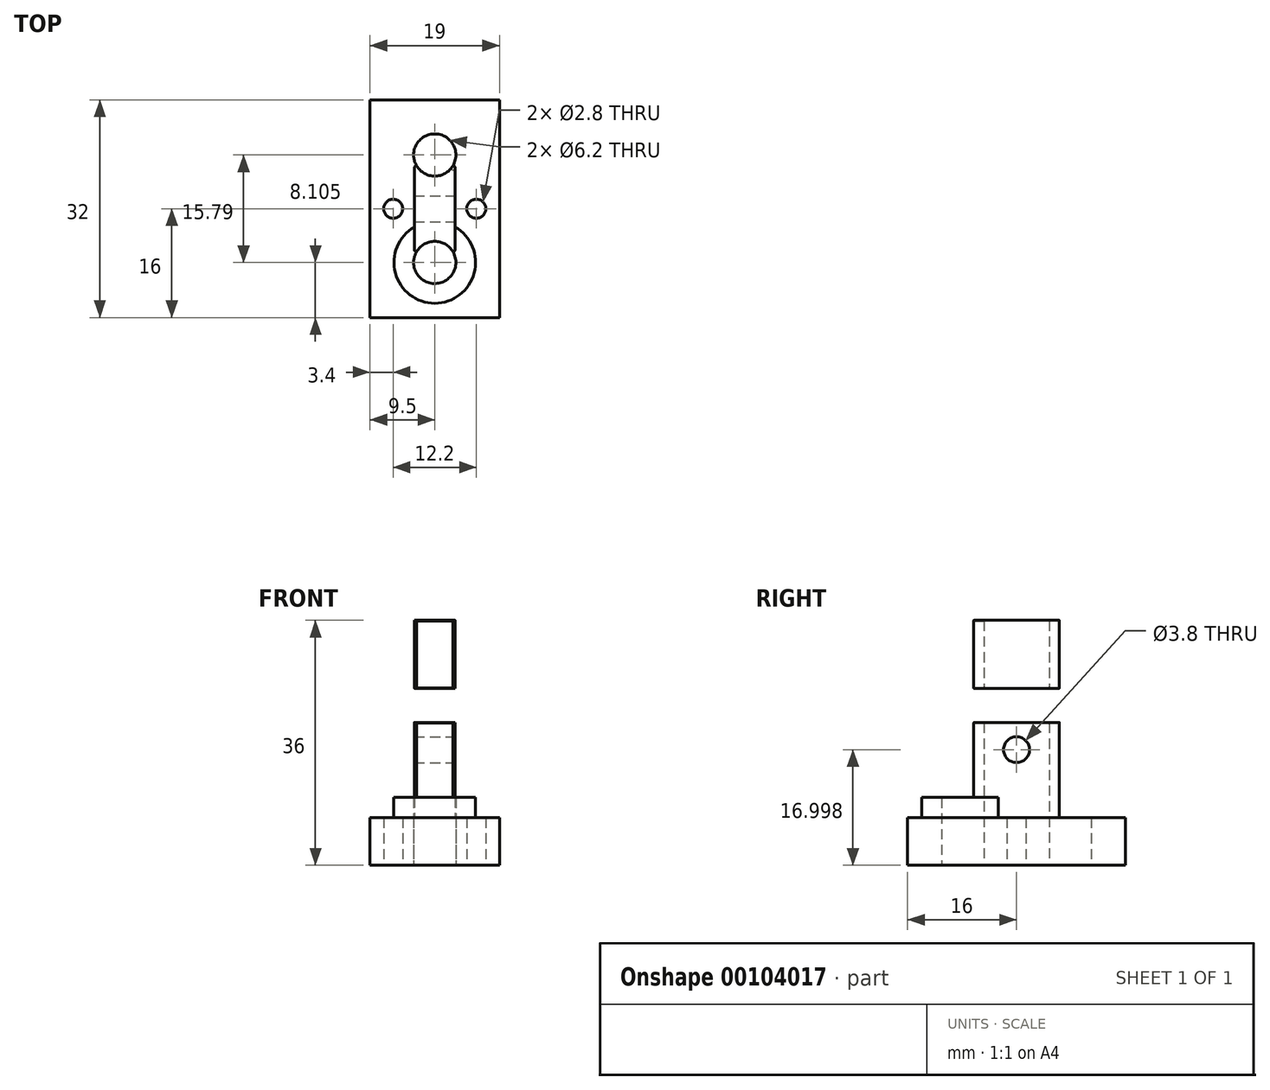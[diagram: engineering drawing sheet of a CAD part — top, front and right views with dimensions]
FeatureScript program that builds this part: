
annotation { "Feature Type Name" : "Feature", "Feature Type Description" : "" }
export const myFeature = defineFeature(function(context is Context, id is Id, definition is map)
    precondition{}
    {
        {
            var Q0;
            Q0=qCreatedBy(makeId("Top.planeOp"),FACE);
            var sketch = newSketch(context, id + "F0", { "sketchPlane" : qUnion([Q0])});
            skCircle(sketch, "E0", {"center": v(0, -7.9) * mm, "radius": 3 * mm});
            skLineSegment(sketch, "E1", {"start": v(-3.1, 0) * mm, "end": v(4.43, 0) * mm, "construction": true});
            skCircle(sketch, "E2.MirrorC", {"center": v(0, 7.9) * mm, "radius": 3 * mm});
            skLineSegment(sketch, "E3", {"start": v(-4.67, -18.12) * mm, "end": v(4.3, -18.12) * mm, "construction": true});
            skCircle(sketch, "E4.MirrorC", {"center": v(0, -28.36) * mm, "radius": 3 * mm, "construction": true});
            skLineSegment(sketch, "E5.MirrorCS", {"start": v(-4.67, 18.12) * mm, "end": v(4.3, 18.12) * mm, "construction": true});
            skLineSegment(sketch, "E6", {"start": v(-3, -7.9) * mm, "end": v(-3, 7.9) * mm});
            skLineSegment(sketch, "E7", {"start": v(3, -7.9) * mm, "end": v(3, 7.9) * mm});
            skArc(sketch, "E8", {"start": v(-3, -2.7) * mm, "mid": v(0, -13.9) * mm, "end": v(3, -2.7) * mm});
            skArc(sketch, "E9.MirrorCS", {"start": v(-3, 2.7) * mm, "mid": v(0, 13.9) * mm, "end": v(3, 2.7) * mm});
            skSolve(sketch);
        }
        {
            var Q0;
            {var subQ5=sQuery(id+"F0.wireOp",EDGE,"E8");Q0=makeQuery(id+"F0.imprint","IMPRINT",FACE,{"disambiguationData":[TD([[makeQuery(id+"F0.imprint","IMPRINT",EDGE,{"derivedFrom":subQ5}),1.0]])]});}
            var Q1;
            {var subQ1=sQuery(id+"F0.wireOp",EDGE,"E6");var subQ5=sQuery(id+"F0.wireOp",EDGE,"E0");var subQ6=makeQuery(id+"F0.imprint","INTERSECT",VERTEX,{"derivedFrom":[subQ5,subQ1]});Q1=makeQuery(id+"F0.imprint","IMPRINT",FACE,{"disambiguationData":[TD([[makeQuery(id+"F0.imprint","IMPRINT",EDGE,{"disambiguationData":[TD([[subQ6,1.0]])],"derivedFrom":subQ5}),-1.0]])]});}
            var Q2;
            {var subQ5=sQuery(id+"F0.wireOp",EDGE,"E9.MirrorCS");Q2=makeQuery(id+"F0.imprint","IMPRINT",FACE,{"disambiguationData":[TD([[makeQuery(id+"F0.imprint","IMPRINT",EDGE,{"derivedFrom":subQ5}),-1.0]])]});}
            extrude(context, id + "F1", {"entities" : qUnion([Q0, Q1, Q2]), "depth" : 10 * mm});
        }
        {
            var Q0;
            {var subQ1=sQuery(id+"F0.wireOp",EDGE,"E6");var subQ5=sQuery(id+"F0.wireOp",EDGE,"E0");var subQ6=makeQuery(id+"F0.imprint","INTERSECT",VERTEX,{"derivedFrom":[subQ5,subQ1]});Q0=makeQuery(id+"F0.imprint","IMPRINT",FACE,{"disambiguationData":[TD([[makeQuery(id+"F0.imprint","IMPRINT",EDGE,{"disambiguationData":[TD([[subQ6,1.0]])],"derivedFrom":subQ5}),-1.0]])]});}
            extrude(context, id + "F2", {"entities" : qUnion([Q0]), "operationType" : NewBodyOperationType.ADD, "depth" : 21 * mm});
        }
        {
            var Q0;
            {var subQ0=sQuery(id+"F0.wireOp",EDGE,"E7");Q0=makeQuery(id+"F2.boolean.opBoolean","MERGE",FACE,{"derivedFrom":[makeQuery(id+"F1.opExtrude","SWEPT_FACE",FACE,{"disambiguationData":[OSD([subQ0])]}),makeQuery(id+"F2.opExtrude","SWEPT_FACE",FACE,{"disambiguationData":[OSD([subQ0])]})]});}
            var sketch = newSketch(context, id + "F3", { "sketchPlane" : qUnion([Q0])});
            skCircle(sketch, "E10", {"center": v(0, 17) * mm, "radius": 1.9 * mm});
            skPoint(sketch, "E10.centerSnap0", {"position": v(0, 21) * mm});
            skCircle(sketch, "E11", {"center": v(0, 17) * mm, "radius": 7.5 * mm, "construction": true});
            skSolve(sketch);
        }
        {
            var Q0;
            Q0=makeQuery(id+"F3.imprint","IMPRINT",FACE,{"disambiguationData":[TD([[makeQuery(id+"F3.imprint","IMPRINT",EDGE,{"derivedFrom":sQuery(id+"F3.wireOp",EDGE,"E10")}),1.0]])]});
            extrude(context, id + "F4", {"entities" : qUnion([Q0]), "operationType" : NewBodyOperationType.REMOVE, "oppositeDirection" : true, "depth" : 25 * mm});
        }
        {
            var Q0;
            Q0=makeQuery(id+"F2.opExtrude","CAP_FACE",FACE,{"disambiguationData":[OSD([sQuery(id+"F0.wireOp",EDGE,"E0"),sQuery(id+"F0.wireOp",EDGE,"E2.MirrorC"),sQuery(id+"F0.wireOp",EDGE,"E6"),sQuery(id+"F0.wireOp",EDGE,"E7")])],"isStart":false});
            extrude(context, id + "F5", {"entities" : qUnion([Q0]), "depth" : 10 * mm});
        }
        {
            var Q0;
            Q0=makeQuery(id+"F5.opExtrude","SWEPT_BODY",BODY,{"disambiguationData":[OSD([sQuery(id+"F0.wireOp",EDGE,"E0"),sQuery(id+"F0.wireOp",EDGE,"E2.MirrorC"),sQuery(id+"F0.wireOp",EDGE,"E6"),sQuery(id+"F0.wireOp",EDGE,"E7")])]});
            transform(context, id + "F6", {"entities" : qUnion([Q0]), "transformType" : TransformType.TRANSLATION_3D, "dx" : 0 * mm, "dy" : 0 * mm, "dz" : 5 * mm, "makeCopy" : false});
        }
        {
            var Q0;
            Q0=makeQuery(id+"F1.opExtrude","CAP_FACE",FACE,{"disambiguationData":[OSD([sQuery(id+"F0.wireOp",EDGE,"E0"),sQuery(id+"F0.wireOp",EDGE,"E2.MirrorC"),sQuery(id+"F0.wireOp",EDGE,"E6"),sQuery(id+"F0.wireOp",EDGE,"E7"),sQuery(id+"F0.wireOp",EDGE,"E8"),sQuery(id+"F0.wireOp",EDGE,"E9.MirrorCS")])],"isStart":true});
            var sketch = newSketch(context, id + "F7", { "sketchPlane" : qUnion([Q0])});
            skLineSegment(sketch, "E12.bottom", {"start": v(9.5, -16) * mm, "end": v(-9.5, -16) * mm});
            skLineSegment(sketch, "E12.top", {"start": v(9.5, 16) * mm, "end": v(-9.5, 16) * mm});
            skLineSegment(sketch, "E12.left", {"start": v(9.5, -16) * mm, "end": v(9.5, 16) * mm});
            skLineSegment(sketch, "E12.right", {"start": v(-9.5, -16) * mm, "end": v(-9.5, 16) * mm});
            skPoint(sketch, "E12.middle", {"position": v(0, 0) * mm});
            skLineSegment(sketch, "E13", {"start": v(0, -16) * mm, "end": v(0, 16) * mm, "construction": true});
            skCircle(sketch, "E14", {"center": v(6.1, 0) * mm, "radius": 1.4 * mm});
            skCircle(sketch, "E15.MirrorC", {"center": v(-6.1, 0) * mm, "radius": 1.4 * mm});
            skSolve(sketch);
        }
        {
            var Q0;
            Q0=makeQuery(id+"F7.imprint","IMPRINT",FACE,{"disambiguationData":[TD([[makeQuery(id+"F7.imprint","IMPRINT",EDGE,{"derivedFrom":sQuery(id+"F7.wireOp",EDGE,"E12.bottom")}),-1.0]])]});
            extrude(context, id + "F8", {"entities" : qUnion([Q0]), "operationType" : NewBodyOperationType.ADD, "oppositeDirection" : true, "depth" : 7 * mm});
        }
        {
            var Q0;
            Q0=makeQuery(id+"F2.opExtrude","SWEPT_EDGE",EDGE,{"disambiguationData":[OSD([sQuery(id+"F0.wireOp",EDGE,"E0"),sQuery(id+"F0.wireOp",EDGE,"E7")])]});
            var Q1;
            Q1=makeQuery(id+"F2.opExtrude","SWEPT_EDGE",EDGE,{"disambiguationData":[OSD([sQuery(id+"F0.wireOp",EDGE,"E0"),sQuery(id+"F0.wireOp",EDGE,"E6")])]});
            var Q2;
            Q2=makeQuery(id+"F2.opExtrude","SWEPT_EDGE",EDGE,{"disambiguationData":[OSD([sQuery(id+"F0.wireOp",EDGE,"E2.MirrorC"),sQuery(id+"F0.wireOp",EDGE,"E7")])]});
            var Q3;
            Q3=makeQuery(id+"F2.opExtrude","SWEPT_EDGE",EDGE,{"disambiguationData":[OSD([sQuery(id+"F0.wireOp",EDGE,"E2.MirrorC"),sQuery(id+"F0.wireOp",EDGE,"E6")])]});
            var Q4;
            Q4=makeQuery(id+"F2.opExtrude","CAP_EDGE",EDGE,{"disambiguationData":[OSD([sQuery(id+"F0.wireOp",EDGE,"E0")])],"isStart":false});
            var Q5;
            Q5=makeQuery(id+"F2.opExtrude","CAP_EDGE",EDGE,{"disambiguationData":[OSD([sQuery(id+"F0.wireOp",EDGE,"E2.MirrorC")])],"isStart":false});
            var Q6;
            Q6=makeQuery(id+"F1.opExtrude","CAP_EDGE",EDGE,{"disambiguationData":[OSD([sQuery(id+"F0.wireOp",EDGE,"E0")])],"isStart":false});
            var Q7;
            Q7=makeQuery(id+"F1.opExtrude","CAP_EDGE",EDGE,{"disambiguationData":[OSD([sQuery(id+"F0.wireOp",EDGE,"E2.MirrorC")])],"isStart":false});
            var Q8;
            Q8=makeQuery(id+"F5.opExtrude","SWEPT_FACE",FACE,{"disambiguationData":[OSD([sQuery(id+"F0.wireOp",EDGE,"E0")])]});
            var Q9;
            Q9=makeQuery(id+"F5.opExtrude","SWEPT_FACE",FACE,{"disambiguationData":[OSD([sQuery(id+"F0.wireOp",EDGE,"E2.MirrorC")])]});
            fillet(context, id + "F9", {"entities" : qUnion([Q0, Q1, Q2, Q3, Q4, Q5, Q6, Q7, Q8, Q9]), "radius" : 0.3 * mm, "tangentPropagation" : true, "allowEdgeOverflow" : false});
        }
        {
            var Q0;
            Q0=sQuery(id+"F0.wireOp",VERTEX,"E0.center");
            var Q1;
            Q1=sQuery(id+"F0.wireOp",VERTEX,"E2.MirrorC.center");
            var Q2;
            Q2=makeQuery(id+"F1.opExtrude","SWEPT_BODY",BODY,{"disambiguationData":[OSD([sQuery(id+"F0.wireOp",EDGE,"E0"),sQuery(id+"F0.wireOp",EDGE,"E2.MirrorC"),sQuery(id+"F0.wireOp",EDGE,"E6"),sQuery(id+"F0.wireOp",EDGE,"E7"),sQuery(id+"F0.wireOp",EDGE,"E8"),sQuery(id+"F0.wireOp",EDGE,"E9.MirrorCS")])]});
            var Q3;
            Q3=makeQuery(id+"F5.opExtrude","SWEPT_BODY",BODY,{"disambiguationData":[OSD([sQuery(id+"F0.wireOp",EDGE,"E0"),sQuery(id+"F0.wireOp",EDGE,"E2.MirrorC"),sQuery(id+"F0.wireOp",EDGE,"E6"),sQuery(id+"F0.wireOp",EDGE,"E7")])]});
            hole(context, id + "F10", {"style" : HoleStyle.SIMPLE, "endStyle" : HoleEndStyle.THROUGH, "oppositeDirection" : true, "holeDiameter" : 6.2 * mm, "locations" : qUnion([Q0, Q1]), "scope" : qUnion([Q2, Q3]), "isTappedThrough" : true});
        }
    });
